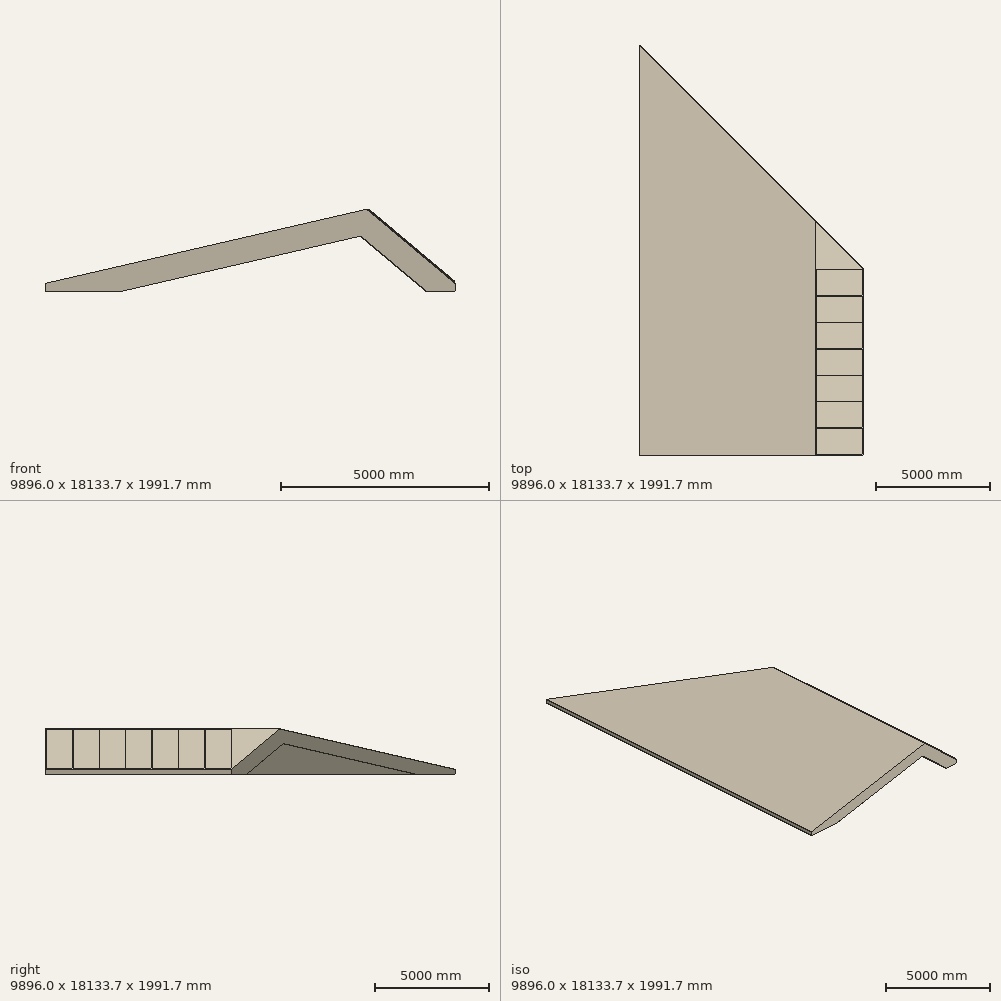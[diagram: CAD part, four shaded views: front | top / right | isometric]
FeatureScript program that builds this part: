
annotation { "Feature Type Name" : "Feature", "Feature Type Description" : "" }
export const myFeature = defineFeature(function(context is Context, id is Id, definition is map)
    precondition{}
    {
        {
            var Q0;
            Q0=qCreatedBy(makeId("Front.planeOp"),FACE);
            var sketch = newSketch(context, id + "F0", { "sketchPlane" : qUnion([Q0])});
            skLineSegment(sketch, "E0", {"start": v(0, 0) * mm, "end": v(8627.05, 1991.71) * mm});
            skLineSegment(sketch, "E1", {"start": v(8627.05, 1991.71) * mm, "end": v(11000.68, 0) * mm});
            skLineSegment(sketch, "E2", {"start": v(11000.68, 0) * mm, "end": v(0, 0) * mm});
            skLineSegment(sketch, "E3", {"start": v(2667.25, 0) * mm, "end": v(8470.54, 1339.8) * mm});
            skLineSegment(sketch, "E4", {"start": v(8470.54, 1339.8) * mm, "end": v(10067.25, 0) * mm});
            skLineSegment(sketch, "E5", {"start": v(866.3, 0) * mm, "end": v(866.3, 200) * mm});
            skLineSegment(sketch, "E6", {"start": v(10762.33, 200) * mm, "end": v(10762.33, 0) * mm});
            skSolve(sketch);
        }
        {
            var Q0;
            {var subQ3=sQuery(id+"F0.wireOp",EDGE,"E3");Q0=makeQuery(id+"F0.imprint","IMPRINT",FACE,{"disambiguationData":[TD([[makeQuery(id+"F0.imprint","IMPRINT",EDGE,{"derivedFrom":subQ3}),1.0]])]});}
            extrude(context, id + "F1", {"entities" : qUnion([Q0]), "oppositeDirection" : true, "depth" : 19000 * mm, "offsetDistance" : 25 * mm});
        }
        {
            var Q0;
            {var subQ0=sQuery(id+"F0.wireOp",EDGE,"E2");Q0=makeQuery(id+"F1.opExtrude","SWEPT_FACE",FACE,{"disambiguationData":[OSD([subQ0]),TDD([makeQuery(id+"F0.imprint","IMPRINT",EDGE,{"disambiguationData":[TD([[makeQuery(id+"F0.imprint","INTERSECT",VERTEX,{"derivedFrom":[subQ0,sQuery(id+"F0.wireOp",EDGE,"E3")]}),-1.0]])],"derivedFrom":subQ0})])]});}
            var sketch = newSketch(context, id + "F2", { "sketchPlane" : qUnion([Q0])});
            skLineSegment(sketch, "E7.bottom", {"start": v(0, -19000) * mm, "end": v(11151.25, -19000) * mm});
            skLineSegment(sketch, "E7.top", {"start": v(0, -7848.75) * mm, "end": v(11151.25, -7848.75) * mm});
            skLineSegment(sketch, "E7.left", {"start": v(0, -19000) * mm, "end": v(0, -7848.75) * mm});
            skLineSegment(sketch, "E7.right", {"start": v(11151.25, -19000) * mm, "end": v(11151.25, -7848.75) * mm});
            skLineSegment(sketch, "E8", {"start": v(0, -19000) * mm, "end": v(11151.25, -7848.75) * mm});
            skSolve(sketch);
        }
        {
            var Q0;
            {var subQ3=sQuery(id+"F2.wireOp",EDGE,"E7.right");Q0=makeQuery(id+"F2.imprint","IMPRINT",FACE,{"disambiguationData":[TD([[makeQuery(id+"F2.imprint","IMPRINT",EDGE,{"derivedFrom":subQ3}),1.0]])]});}
            var Q1;
            {var subQ0=sQuery(id+"F2.wireOp",EDGE,"E7.bottom");var subQ1=sQuery(id+"F0.wireOp",EDGE,"E2");var subQ2=makeQuery(id+"F1.opExtrude","SWEPT_EDGE",EDGE,{"disambiguationData":[OSD([subQ1,sQuery(id+"F0.wireOp",EDGE,"E3")])]});var subQ3=makeQuery(id+"F2.imprint","INTERSECT",VERTEX,{"derivedFrom":[subQ2,subQ0]});var subQ4=makeQuery(id+"F1.opExtrude","SWEPT_EDGE",EDGE,{"disambiguationData":[OSD([subQ1,sQuery(id+"F0.wireOp",EDGE,"E5")])]});var subQ5=makeQuery(id+"F2.imprint","INTERSECT",VERTEX,{"derivedFrom":[subQ4,subQ0]});Q1=makeQuery(id+"F2.imprint","IMPRINT",FACE,{"disambiguationData":[TD([[makeQuery(id+"F2.imprint","IMPRINT",EDGE,{"disambiguationData":[TD([[subQ3,-1.0],[subQ5,1.0]])],"derivedFrom":subQ0}),-1.0]])]});}
            extrude(context, id + "F3", {"entities" : qUnion([Q0, Q1]), "operationType" : NewBodyOperationType.REMOVE, "endBound" : BoundingType.THROUGH_ALL, "oppositeDirection" : true, "depth" : 25 * mm, "offsetDistance" : 25 * mm});
        }
        {
            var Q0;
            Q0=makeQuery(id+"F1.opExtrude","SWEPT_FACE",FACE,{"disambiguationData":[OSD([sQuery(id+"F0.wireOp",EDGE,"E1")])]});
            var sketch = newSketch(context, id + "F4", { "sketchPlane" : qUnion([Q0])});
            skLineSegment(sketch, "E9.bottom", {"start": v(8065.87, 50) * mm, "end": v(5365.87, 50) * mm});
            skLineSegment(sketch, "E9.top", {"start": v(8065.87, 1200) * mm, "end": v(5365.87, 1200) * mm});
            skLineSegment(sketch, "E9.left", {"start": v(8065.87, 50) * mm, "end": v(8065.87, 1200) * mm});
            skLineSegment(sketch, "E9.right", {"start": v(5365.87, 50) * mm, "end": v(5365.87, 1200) * mm});
            skLineSegment(sketch, "E10.0.1.0", {"start": v(8065.87, 2370) * mm, "end": v(5365.87, 2370) * mm});
            skLineSegment(sketch, "E10.0.1.1", {"start": v(8065.87, 1220) * mm, "end": v(8065.87, 2370) * mm});
            skLineSegment(sketch, "E10.0.1.2", {"start": v(8065.87, 1220) * mm, "end": v(5365.87, 1220) * mm});
            skLineSegment(sketch, "E10.0.1.3", {"start": v(5365.87, 1220) * mm, "end": v(5365.87, 2370) * mm});
            skLineSegment(sketch, "E10.direction1", {"start": v(6815.87, 50) * mm, "end": v(5515.87, 50) * mm, "construction": true});
            skLineSegment(sketch, "E10.direction2", {"start": v(6815.87, 50) * mm, "end": v(6815.87, 1500) * mm, "construction": true});
            skLineSegment(sketch, "E11.0.0.2", {"start": v(8065.87, 3540) * mm, "end": v(5365.87, 3540) * mm});
            skLineSegment(sketch, "E11.3.0.2", {"start": v(8065.87, 2390) * mm, "end": v(8065.87, 3540) * mm});
            skLineSegment(sketch, "E11.6.0.2", {"start": v(8065.87, 2390) * mm, "end": v(5365.87, 2390) * mm});
            skLineSegment(sketch, "E11.9.0.2", {"start": v(5365.87, 2390) * mm, "end": v(5365.87, 3540) * mm});
            skLineSegment(sketch, "E11.0.0.3", {"start": v(8065.87, 4710) * mm, "end": v(5365.87, 4710) * mm});
            skLineSegment(sketch, "E11.3.0.3", {"start": v(8065.87, 3560) * mm, "end": v(8065.87, 4710) * mm});
            skLineSegment(sketch, "E11.6.0.3", {"start": v(8065.87, 3560) * mm, "end": v(5365.87, 3560) * mm});
            skLineSegment(sketch, "E11.9.0.3", {"start": v(5365.87, 3560) * mm, "end": v(5365.87, 4710) * mm});
            skLineSegment(sketch, "E11.0.0.4", {"start": v(8065.87, 5880) * mm, "end": v(5365.87, 5880) * mm});
            skLineSegment(sketch, "E11.3.0.4", {"start": v(8065.87, 4730) * mm, "end": v(8065.87, 5880) * mm});
            skLineSegment(sketch, "E11.6.0.4", {"start": v(8065.87, 4730) * mm, "end": v(5365.87, 4730) * mm});
            skLineSegment(sketch, "E11.9.0.4", {"start": v(5365.87, 4730) * mm, "end": v(5365.87, 5880) * mm});
            skLineSegment(sketch, "E11.0.0.5", {"start": v(8065.87, 7050) * mm, "end": v(5365.87, 7050) * mm});
            skLineSegment(sketch, "E11.3.0.5", {"start": v(8065.87, 5900) * mm, "end": v(8065.87, 7050) * mm});
            skLineSegment(sketch, "E11.6.0.5", {"start": v(8065.87, 5900) * mm, "end": v(5365.87, 5900) * mm});
            skLineSegment(sketch, "E11.9.0.5", {"start": v(5365.87, 5900) * mm, "end": v(5365.87, 7050) * mm});
            skLineSegment(sketch, "E12.0.0.6", {"start": v(8065.87, 8220) * mm, "end": v(5365.87, 8220) * mm});
            skLineSegment(sketch, "E12.3.0.6", {"start": v(8065.87, 7070) * mm, "end": v(8065.87, 8220) * mm});
            skLineSegment(sketch, "E12.6.0.6", {"start": v(8065.87, 7070) * mm, "end": v(5365.87, 7070) * mm});
            skLineSegment(sketch, "E12.9.0.6", {"start": v(5365.87, 7070) * mm, "end": v(5365.87, 8220) * mm});
            skLineSegment(sketch, "E13", {"start": v(8115.87, 0) * mm, "end": v(8115.87, 8237.67) * mm});
            skSolve(sketch);
        }
        {
            var Q0;
            Q0=makeQuery(id+"F4.imprint","IMPRINT",FACE,{"disambiguationData":[TD([[makeQuery(id+"F4.imprint","IMPRINT",EDGE,{"derivedFrom":sQuery(id+"F4.wireOp",EDGE,"E9.bottom")}),-1.0]])]});
            var Q1;
            Q1=makeQuery(id+"F4.imprint","IMPRINT",FACE,{"disambiguationData":[TD([[makeQuery(id+"F4.imprint","IMPRINT",EDGE,{"derivedFrom":sQuery(id+"F4.wireOp",EDGE,"E10.0.1.0")}),1.0]])]});
            var Q2;
            Q2=makeQuery(id+"F4.imprint","IMPRINT",FACE,{"disambiguationData":[TD([[makeQuery(id+"F4.imprint","IMPRINT",EDGE,{"derivedFrom":sQuery(id+"F4.wireOp",EDGE,"E10.1.0.0")}),1.0]])]});
            var Q3;
            Q3=makeQuery(id+"F4.imprint","IMPRINT",FACE,{"disambiguationData":[TD([[makeQuery(id+"F4.imprint","IMPRINT",EDGE,{"derivedFrom":sQuery(id+"F4.wireOp",EDGE,"E10.1.1.0")}),1.0]])]});
            var Q4;
            Q4=makeQuery(id+"F4.imprint","IMPRINT",FACE,{"disambiguationData":[TD([[makeQuery(id+"F4.imprint","IMPRINT",EDGE,{"derivedFrom":sQuery(id+"F4.wireOp",EDGE,"E11.0.0.2")}),1.0]])]});
            var Q5;
            Q5=makeQuery(id+"F4.imprint","IMPRINT",FACE,{"disambiguationData":[TD([[makeQuery(id+"F4.imprint","IMPRINT",EDGE,{"derivedFrom":sQuery(id+"F4.wireOp",EDGE,"E11.0.0.3")}),1.0]])]});
            var Q6;
            Q6=makeQuery(id+"F4.imprint","IMPRINT",FACE,{"disambiguationData":[TD([[makeQuery(id+"F4.imprint","IMPRINT",EDGE,{"derivedFrom":sQuery(id+"F4.wireOp",EDGE,"E11.0.0.4")}),1.0]])]});
            var Q7;
            Q7=makeQuery(id+"F4.imprint","IMPRINT",FACE,{"disambiguationData":[TD([[makeQuery(id+"F4.imprint","IMPRINT",EDGE,{"derivedFrom":sQuery(id+"F4.wireOp",EDGE,"E11.0.1.2")}),1.0]])]});
            var Q8;
            Q8=makeQuery(id+"F4.imprint","IMPRINT",FACE,{"disambiguationData":[TD([[makeQuery(id+"F4.imprint","IMPRINT",EDGE,{"derivedFrom":sQuery(id+"F4.wireOp",EDGE,"E11.0.1.3")}),1.0]])]});
            var Q9;
            Q9=makeQuery(id+"F4.imprint","IMPRINT",FACE,{"disambiguationData":[TD([[makeQuery(id+"F4.imprint","IMPRINT",EDGE,{"derivedFrom":sQuery(id+"F4.wireOp",EDGE,"E11.0.1.4")}),1.0]])]});
            var Q10;
            Q10=makeQuery(id+"F4.imprint","IMPRINT",FACE,{"disambiguationData":[TD([[makeQuery(id+"F4.imprint","IMPRINT",EDGE,{"derivedFrom":sQuery(id+"F4.wireOp",EDGE,"E11.0.1.5")}),1.0]])]});
            var Q11;
            Q11=makeQuery(id+"F4.imprint","IMPRINT",FACE,{"disambiguationData":[TD([[makeQuery(id+"F4.imprint","IMPRINT",EDGE,{"derivedFrom":sQuery(id+"F4.wireOp",EDGE,"E11.0.0.5")}),1.0]])]});
            var Q12;
            Q12=makeQuery(id+"F4.imprint","IMPRINT",FACE,{"disambiguationData":[TD([[makeQuery(id+"F4.imprint","IMPRINT",EDGE,{"derivedFrom":sQuery(id+"F4.wireOp",EDGE,"E12.0.0.6")}),1.0]])]});
            extrude(context, id + "F5", {"entities" : qUnion([Q0, Q1, Q2, Q3, Q4, Q5, Q6, Q7, Q8, Q9, Q10, Q11, Q12]), "operationType" : NewBodyOperationType.ADD, "depth" : 25 * mm, "offsetDistance" : 25 * mm});
        }
    });
